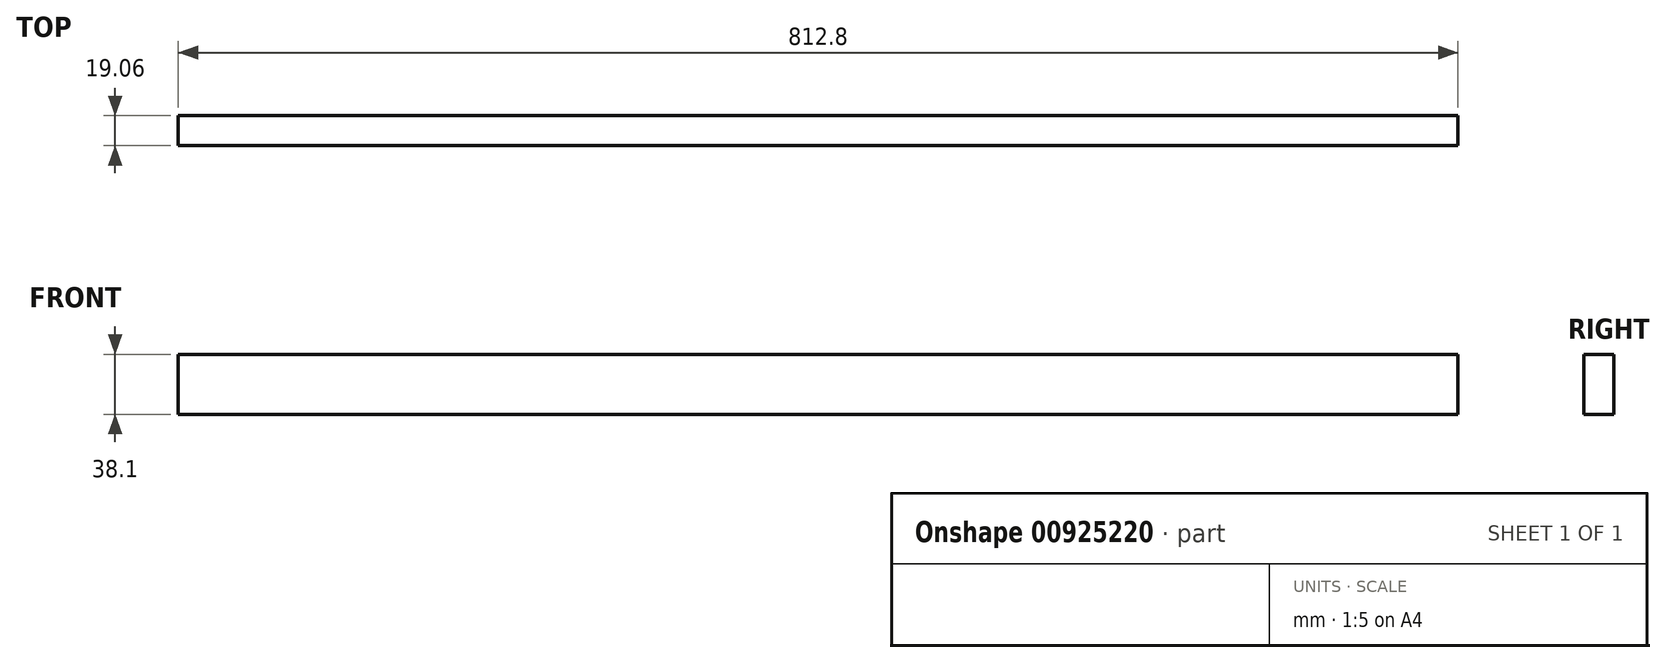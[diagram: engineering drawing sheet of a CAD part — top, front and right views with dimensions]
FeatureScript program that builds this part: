
annotation { "Feature Type Name" : "Feature", "Feature Type Description" : "" }
export const myFeature = defineFeature(function(context is Context, id is Id, definition is map)
    precondition{}
    {
        {
            var Q0;
            Q0=qCreatedBy(makeId("Right.planeOp"),FACE);
            var sketch = newSketch(context, id + "F0", { "sketchPlane" : qUnion([Q0])});
            skLineSegment(sketch, "E0.bottom", {"start": v(9.53, -19.05) * mm, "end": v(-9.53, -19.05) * mm});
            skLineSegment(sketch, "E0.top", {"start": v(9.52, 19.05) * mm, "end": v(-9.52, 19.05) * mm});
            skLineSegment(sketch, "E0.left", {"start": v(9.52, -19.05) * mm, "end": v(9.53, 19.05) * mm});
            skLineSegment(sketch, "E0.right", {"start": v(-9.53, -19.05) * mm, "end": v(-9.52, 19.05) * mm});
            skPoint(sketch, "E0.middle", {"position": v(0, 0) * mm});
            skSolve(sketch);
        }
        {
            var Q0;
            Q0=makeQuery(id+"F0.imprint","IMPRINT",FACE,{"disambiguationData":[TD([[makeQuery(id+"F0.imprint","IMPRINT",EDGE,{"derivedFrom":sQuery(id+"F0.wireOp",EDGE,"E0.bottom")}),-1.0]])]});
            extrude(context, id + "F1", {"entities" : qUnion([Q0]), "depth" : 812.8 * mm, "offsetDistance" : 25.4 * mm});
        }
    });
